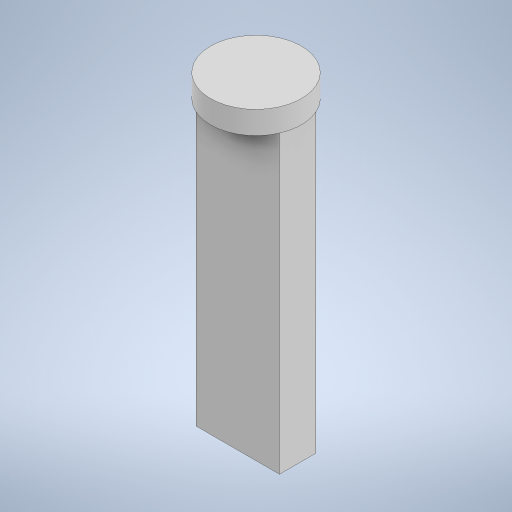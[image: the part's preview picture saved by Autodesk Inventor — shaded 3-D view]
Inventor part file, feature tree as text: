
AUTODESK INVENTOR PART (.ipt)
format: ipt  version: 2023 (Build 270158000, 158)  size: 229,376 bytes
history: native  units: mm
features: extrude x2, sketch x2, projected_geometry x1
ambient origin geometry x8: Origin, YZ Plane, XZ Plane, XY Plane, X Axis, Y Axis, Z Axis, Center Point
bodies: Solid1 (feature_tree)
feature tree (5):
  extrude  "Extrusion1"  Depth=5.0mm TaperAngle=0.0deg
  extrude  "Extrusion2"  Depth=65.0mm TaperAngle=0.0deg
  sketch  "Sketch1"  dims[d0=20.0mm d1=5.0mm d2=0.0mm]
  sketch  "Sketch2"  dims[d3=8.0mm d5=65.0mm d6=0.0mm d7=0.0mm d8=0.0mm d9=0.0mm d10=0.0mm]
  projected_geometry  "Projected Loop1"
